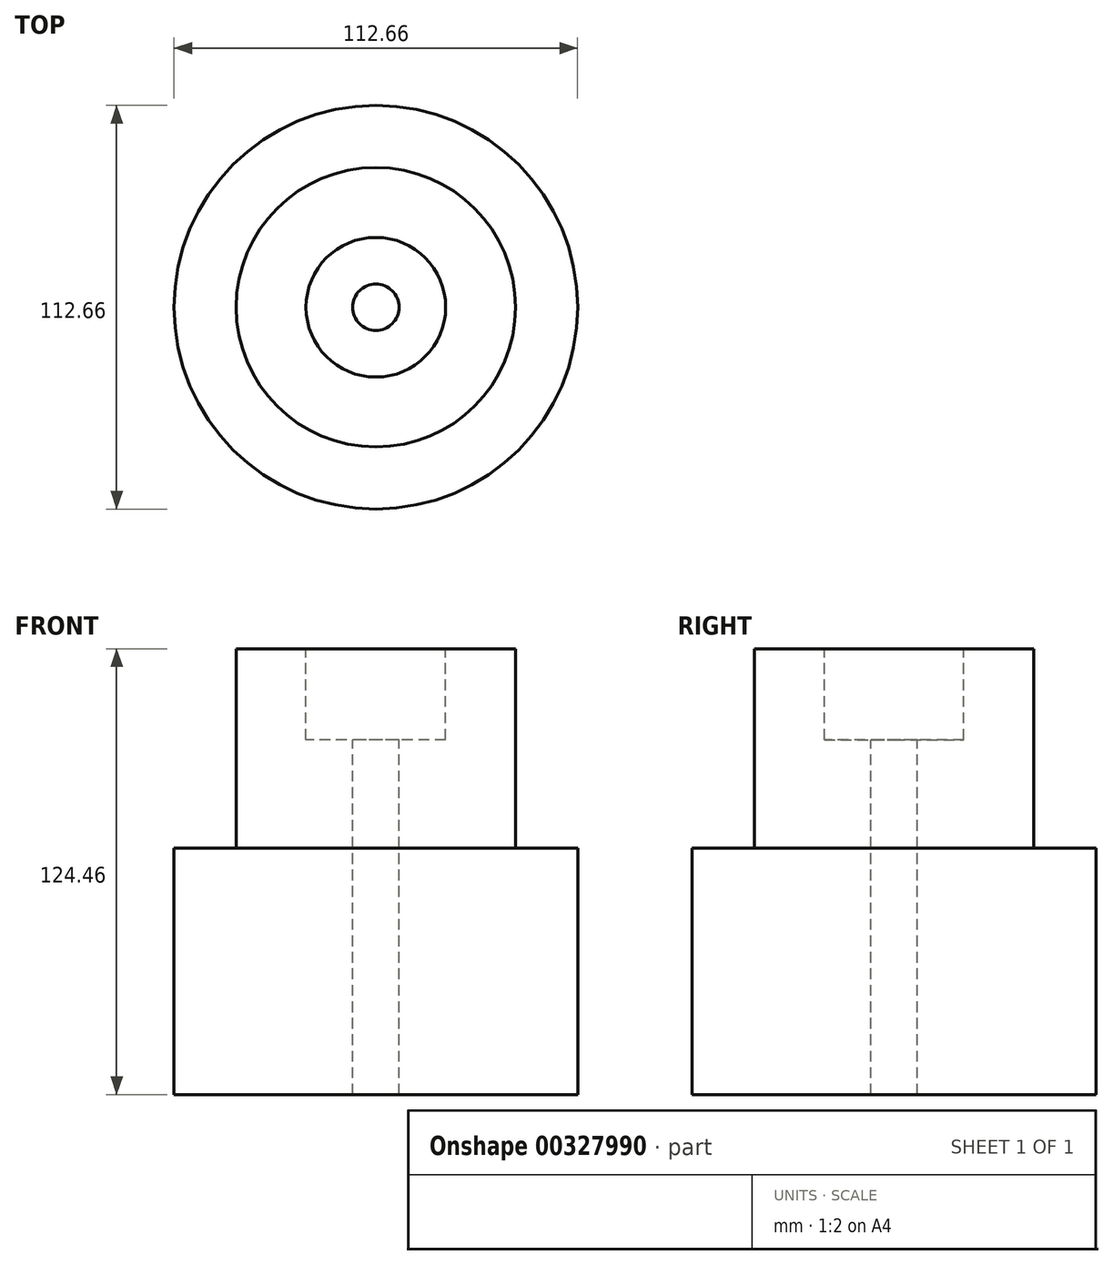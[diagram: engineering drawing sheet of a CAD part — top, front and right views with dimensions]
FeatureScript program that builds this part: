
annotation { "Feature Type Name" : "Feature", "Feature Type Description" : "" }
export const myFeature = defineFeature(function(context is Context, id is Id, definition is map)
    precondition{}
    {
        {
            var Q0;
            Q0=qCreatedBy(makeId("Top.planeOp"),FACE);
            var sketch = newSketch(context, id + "F0", { "sketchPlane" : qUnion([Q0])});
            skCircle(sketch, "E0", {"center": v(0, 0) * mm, "radius": 39 * mm});
            skSolve(sketch);
        }
        {
            var Q0;
            Q0 = qSketchRegion(id + "F0", true);
            extrude(context, id + "F1", {"entities" : qUnion([Q0]), "depth" : 55.63 * mm});
        }
        {
            var Q0;
            Q0=makeQuery(id+"F1.opExtrude","CAP_FACE",FACE,{"disambiguationData":[OSD([sQuery(id+"F0.wireOp",EDGE,"E0")])],"isStart":false});
            var sketch = newSketch(context, id + "F2", { "sketchPlane" : qUnion([Q0])});
            skCircle(sketch, "E1", {"center": v(0, 0) * mm, "radius": 21.47 * mm});
            skSolve(sketch);
        }
        {
            var Q0;
            Q0 = qSketchRegion(id + "F2", true);
            extrude(context, id + "F3", {"entities" : qUnion([Q0]), "operationType" : NewBodyOperationType.ADD, "oppositeDirection" : true, "depth" : 29.46 * mm});
        }
        {
            var Q0;
            Q0=makeQuery(id+"F1.opExtrude","CAP_FACE",FACE,{"disambiguationData":[OSD([sQuery(id+"F0.wireOp",EDGE,"E0")])],"isStart":false});
            var sketch = newSketch(context, id + "F4", { "sketchPlane" : qUnion([Q0])});
            skCircle(sketch, "E2", {"center": v(0, 0) * mm, "radius": 19.5 * mm});
            skSolve(sketch);
        }
        {
            var Q0;
            Q0 = qSketchRegion(id + "F4", true);
            extrude(context, id + "F5", {"entities" : qUnion([Q0]), "operationType" : NewBodyOperationType.REMOVE, "oppositeDirection" : true, "depth" : 25.4 * mm});
        }
        {
            var Q0;
            Q0=makeQuery(id+"F1.opExtrude","CAP_FACE",FACE,{"disambiguationData":[OSD([sQuery(id+"F0.wireOp",EDGE,"E0")])],"isStart":true});
            var sketch = newSketch(context, id + "F6", { "sketchPlane" : qUnion([Q0])});
            skCircle(sketch, "E3", {"center": v(0, 0) * mm, "radius": 56.33 * mm});
            skSolve(sketch);
        }
        {
            var Q0;
            Q0 = qSketchRegion(id + "F6", true);
            extrude(context, id + "F7", {"entities" : qUnion([Q0]), "operationType" : NewBodyOperationType.ADD, "depth" : 68.83 * mm});
        }
        {
            var Q0;
            Q0=makeQuery(id+"F5.boolean.opBoolean","COPY",FACE,{"derivedFrom":makeQuery(id+"F5.opExtrude","CAP_FACE",FACE,{"disambiguationData":[OSD([sQuery(id+"F4.wireOp",EDGE,"E2")])],"isStart":false})});
            var sketch = newSketch(context, id + "F8", { "sketchPlane" : qUnion([Q0])});
            skCircle(sketch, "E4", {"center": v(0, 0) * mm, "radius": 6.5 * mm});
            skSolve(sketch);
        }
        {
            var Q0;
            Q0 = qSketchRegion(id + "F8", true);
            extrude(context, id + "F9", {"entities" : qUnion([Q0]), "operationType" : NewBodyOperationType.REMOVE, "oppositeDirection" : true, "depth" : 169.16 * mm});
        }
    });
